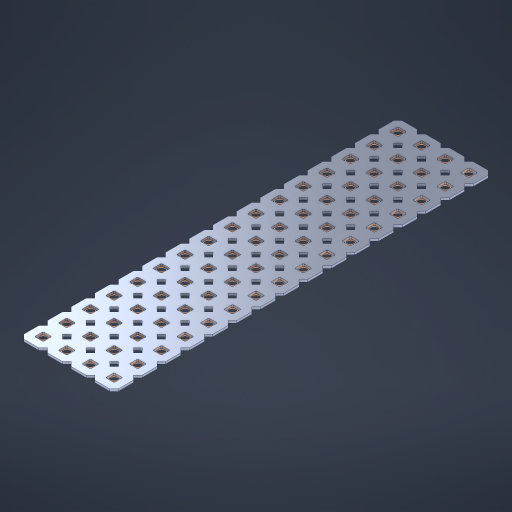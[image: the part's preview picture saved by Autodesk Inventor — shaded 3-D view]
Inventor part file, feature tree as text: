
AUTODESK INVENTOR PART (.ipt)
format: ipt  version: 2023 (Build 270158000, 158)  size: 1,002,496 bytes
history: native  units: in
note: dims shown in document units (in); Inventor stores cm internally (conversion verified against a paired STEP export)
features: other x65, extrude x63, sketch x2, pattern_linear x1
ambient origin geometry x8: Origin, YZ Plane, XZ Plane, XY Plane, X Axis, Y Axis, Z Axis, Center Point
bodies: Solid1 (feature_tree), Body (feature_tree)
feature tree (131):
  pattern_linear  "Rectangular Pattern1"  Spacing1=0.09in  [1 undecoded]
  sketch  "Sketch1"  dims[d1=0.5in]
  sketch  "Sketch2"  dims[d2=0.182in d3=0.09in d4=0.09in d5=0.09in d6=0.09in d7=0.09in d8=0.09in d9=0.09in d10=0.09in d11=0.02in d13=0.0in d14=0.172in d15=0.0625in d16=0.0in d19=0.5in d22=0.5in]
  other  "Srf1"
  other  "Srf126"
  other  "Srf127"
  other  "Srf128"
  other  "Srf129"
  other  "Srf130"
  other  "Srf131"
  other  "Srf250"
  other  "Srf251"
  other  "Srf252"
  other  "Srf253"
  other  "Srf254"
  other  "Srf255"
  other  "Srf256"
  other  "Srf257"
  other  "Srf258"
  other  "Srf268"
  other  "Srf269"
  other  "Srf270"
  other  "Srf271"
  other  "Srf272"
  other  "Srf273"
  other  "Srf274"
  other  "Srf275"
  other  "Srf276"
  other  "Srf277"
  other  "Srf278"
  other  "Srf279"
  other  "Srf280"
  other  "Srf281"
  other  "Srf282"
  other  "Srf283"
  other  "Srf293"
  other  "Srf294"
  other  "Srf295"
  other  "Srf296"
  other  "Srf297"
  other  "Srf298"
  other  "Srf299"
  other  "Srf300"
  other  "Srf301"
  other  "Srf302"
  other  "Srf303"
  other  "Srf304"
  other  "Srf305"
  other  "Srf306"
  other  "Srf307"
  other  "Srf308"
  other  "Srf318"
  other  "Srf319"
  other  "Srf320"
  other  "Srf321"
  other  "Srf322"
  other  "Srf323"
  other  "Srf324"
  other  "Srf325"
  other  "Srf326"
  other  "Srf327"
  other  "Srf328"
  other  "Srf329"
  other  "Srf330"
  other  "Srf331"
  other  "Srf332"
  other  "Srf333"
  other  "Circle"
  extrude  "ExtrusionSrf126"  Depth=0.09in
  extrude  "ExtrusionSrf127"  Depth=0.09in
  extrude  "ExtrusionSrf128"  Depth=0.09in
  extrude  "ExtrusionSrf129"  Depth=0.09in
  extrude  "ExtrusionSrf130"  Depth=0.09in
  extrude  "ExtrusionSrf131"  Depth=0.09in
  extrude  "ExtrusionSrf250"  Depth=0.09in
  extrude  "ExtrusionSrf251"  Depth=0.02in
  extrude  "ExtrusionSrf252"  TaperAngle=0.0deg  [1 undecoded]
  extrude  "ExtrusionSrf253"  Depth=0.5in
  extrude  "ExtrusionSrf254"  Depth=0.5in TaperAngle=0.0deg
  extrude  "ExtrusionSrf255"  Depth=0.5in
  extrude  "ExtrusionSrf256"  Depth=0.5in
  extrude  "ExtrusionSrf257"  [1 undecoded]
  extrude  "ExtrusionSrf258"  [1 undecoded]
  extrude  "ExtrusionSrf268"  [1 undecoded]
  extrude  "ExtrusionSrf269"  [1 undecoded]
  extrude  "ExtrusionSrf270"  [1 undecoded]
  extrude  "ExtrusionSrf271"  [1 undecoded]
  extrude  "ExtrusionSrf272"  [1 undecoded]
  extrude  "ExtrusionSrf273"  [1 undecoded]
  extrude  "ExtrusionSrf274"  [1 undecoded]
  extrude  "ExtrusionSrf275"  [1 undecoded]
  extrude  "ExtrusionSrf276"  [1 undecoded]
  extrude  "ExtrusionSrf277"  [1 undecoded]
  extrude  "ExtrusionSrf278"  [1 undecoded]
  extrude  "ExtrusionSrf279"  [1 undecoded]
  extrude  "ExtrusionSrf280"  [1 undecoded]
  extrude  "ExtrusionSrf281"  [1 undecoded]
  extrude  "ExtrusionSrf282"  [1 undecoded]
  extrude  "ExtrusionSrf283"  [1 undecoded]
  extrude  "ExtrusionSrf293"  [1 undecoded]
  extrude  "ExtrusionSrf294"  [1 undecoded]
  extrude  "ExtrusionSrf295"  [1 undecoded]
  extrude  "ExtrusionSrf296"  [1 undecoded]
  extrude  "ExtrusionSrf297"  [1 undecoded]
  extrude  "ExtrusionSrf298"  [1 undecoded]
  extrude  "ExtrusionSrf299"  [1 undecoded]
  extrude  "ExtrusionSrf300"  [1 undecoded]
  extrude  "ExtrusionSrf301"  [1 undecoded]
  extrude  "ExtrusionSrf302"  [1 undecoded]
  extrude  "ExtrusionSrf303"  [1 undecoded]
  extrude  "ExtrusionSrf304"  [1 undecoded]
  extrude  "ExtrusionSrf305"  [1 undecoded]
  extrude  "ExtrusionSrf306"  [1 undecoded]
  extrude  "ExtrusionSrf307"  [1 undecoded]
  extrude  "ExtrusionSrf308"  [1 undecoded]
  extrude  "ExtrusionSrf318"  [1 undecoded]
  extrude  "ExtrusionSrf319"  [1 undecoded]
  extrude  "ExtrusionSrf320"  [1 undecoded]
  extrude  "ExtrusionSrf321"  [1 undecoded]
  extrude  "ExtrusionSrf322"  [1 undecoded]
  extrude  "ExtrusionSrf323"  [1 undecoded]
  extrude  "ExtrusionSrf324"  [1 undecoded]
  extrude  "ExtrusionSrf325"  [1 undecoded]
  extrude  "ExtrusionSrf326"  [1 undecoded]
  extrude  "ExtrusionSrf327"  [1 undecoded]
  extrude  "ExtrusionSrf328"  [1 undecoded]
  extrude  "ExtrusionSrf329"  [1 undecoded]
  extrude  "ExtrusionSrf330"  [1 undecoded]
  extrude  "ExtrusionSrf331"  [1 undecoded]
  extrude  "ExtrusionSrf332"  [1 undecoded]
  extrude  "ExtrusionSrf333"  [1 undecoded]
note: 52 required parameter values undecoded (feature->parameter linkage not recoverable at this tier; creation-order binding heuristic only, values carry confidence <= 0.55)
